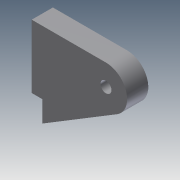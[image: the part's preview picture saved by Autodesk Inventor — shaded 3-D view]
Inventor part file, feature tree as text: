
AUTODESK INVENTOR PART (.ipt)
format: ipt  version: 2011 (Build 150239000, 239)  size: 81,920 bytes
history: native  units: in
note: dims shown in document units (in); Inventor stores cm internally (conversion verified against a paired STEP export)
features: extrude x1, sketch x1
ambient origin geometry x8: Origin, YZ Plane, XZ Plane, XY Plane, X Axis, Y Axis, Z Axis, Center Point
bodies: Solid1 (feature_tree)
feature tree (2):
  extrude  "Extrusion1"  Depth=1.5in
  sketch  "Sketch1"  dims[d0=0.25in d1=1.5in d2=1.75in d3=0.25in d4=0.5in d5=1.504in d6=0.2598in d7=0.25in d8=0.5in d9=0.0in]
